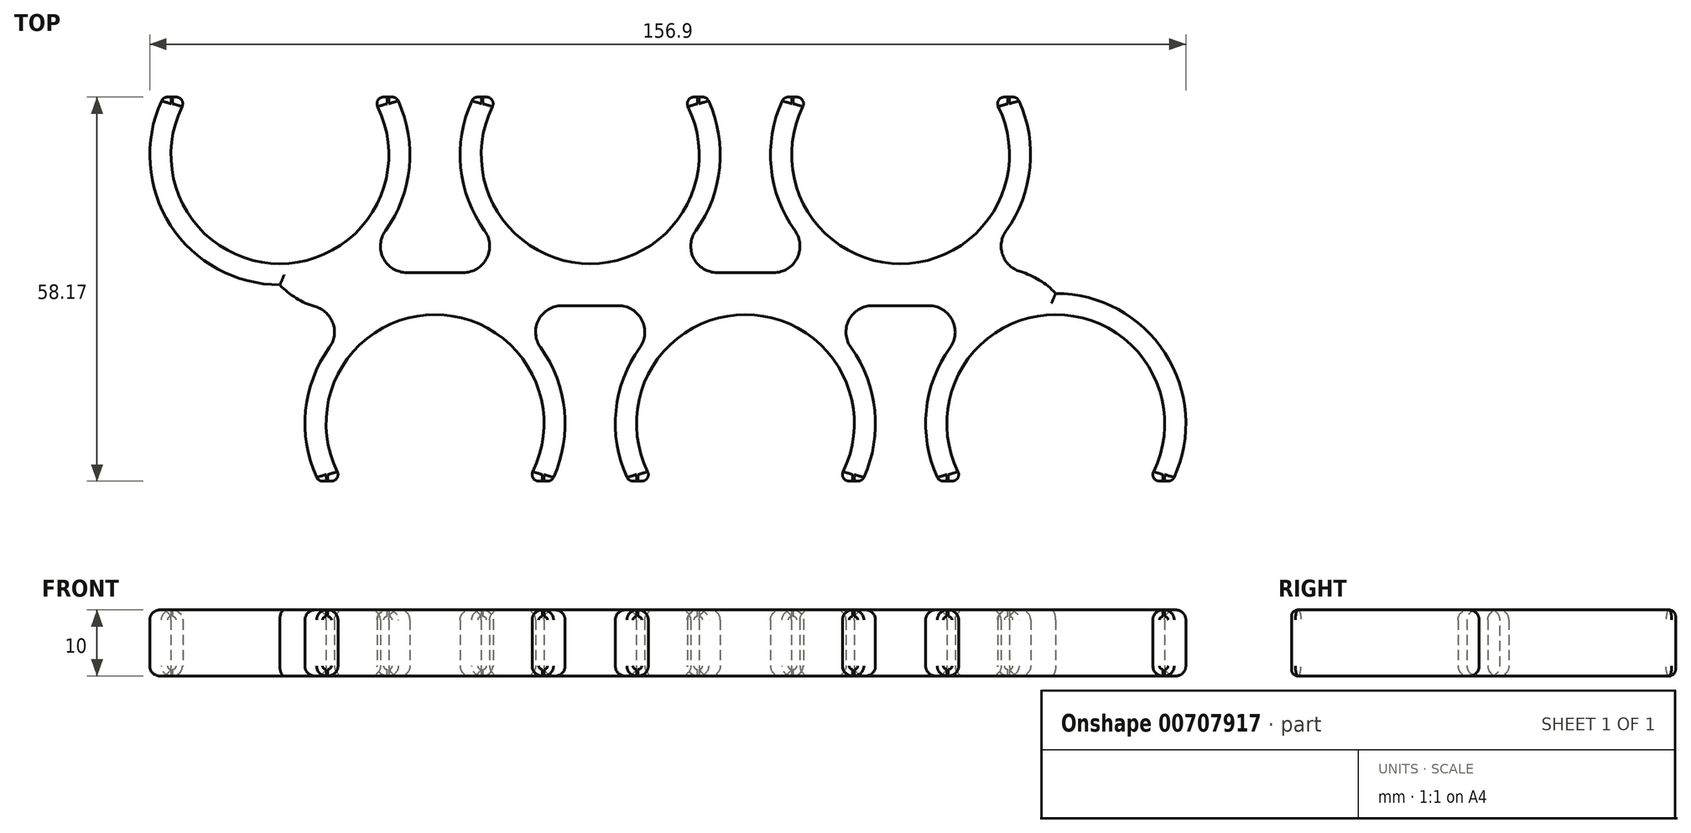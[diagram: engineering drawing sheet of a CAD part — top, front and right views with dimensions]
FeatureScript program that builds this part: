
annotation { "Feature Type Name" : "Feature", "Feature Type Description" : "" }
export const myFeature = defineFeature(function(context is Context, id is Id, definition is map)
    precondition{}
    {
        {
            var Q0;
            Q0=qCreatedBy(makeId("Top.planeOp"),FACE);
            var sketch = newSketch(context, id + "F0", { "sketchPlane" : qUnion([Q0])});
            skArc(sketch, "E0", {"start": v(14, -8.73) * mm, "mid": v(0, 16.5) * mm, "end": v(-14, -8.73) * mm});
            skArc(sketch, "E1", {"start": v(17.66, -8.73) * mm, "mid": v(0, 19.7) * mm, "end": v(-17.66, -8.73) * mm});
            skLineSegment(sketch, "E2", {"start": v(-17.66, -8.73) * mm, "end": v(-14, -8.73) * mm});
            skLineSegment(sketch, "E3", {"start": v(14, -8.73) * mm, "end": v(17.66, -8.73) * mm});
            skArc(sketch, "E4", {"start": v(61, -8.73) * mm, "mid": v(47, 16.5) * mm, "end": v(33, -8.73) * mm});
            skArc(sketch, "E5", {"start": v(64.66, -8.73) * mm, "mid": v(47, 19.7) * mm, "end": v(29.34, -8.73) * mm});
            skLineSegment(sketch, "E6", {"start": v(29.34, -8.73) * mm, "end": v(33, -8.73) * mm});
            skLineSegment(sketch, "E7", {"start": v(61, -8.73) * mm, "end": v(64.66, -8.73) * mm});
            skLineSegment(sketch, "E8", {"start": v(0, 0) * mm, "end": v(47, 0) * mm, "construction": true});
            skArc(sketch, "E9", {"start": v(9.5, 49.44) * mm, "mid": v(23.5, 24.2) * mm, "end": v(37.5, 49.44) * mm});
            skArc(sketch, "E10", {"start": v(5.84, 49.44) * mm, "mid": v(23.5, 21) * mm, "end": v(41.16, 49.44) * mm});
            skLineSegment(sketch, "E11", {"start": v(41.16, 49.44) * mm, "end": v(37.5, 49.44) * mm});
            skLineSegment(sketch, "E12", {"start": v(9.5, 49.44) * mm, "end": v(5.84, 49.44) * mm});
            skLineSegment(sketch, "E13", {"start": v(47, 0) * mm, "end": v(23.5, 40.7) * mm, "construction": true});
            skLineSegment(sketch, "E14", {"start": v(23.5, 40.7) * mm, "end": v(0, 0) * mm, "construction": true});
            skArc(sketch, "E15", {"start": v(-33, -8.73) * mm, "mid": v(-47, 16.5) * mm, "end": v(-61, -8.73) * mm});
            skArc(sketch, "E16", {"start": v(-29.34, -8.73) * mm, "mid": v(-47, 19.7) * mm, "end": v(-64.66, -8.73) * mm});
            skLineSegment(sketch, "E17", {"start": v(-64.66, -8.73) * mm, "end": v(-61, -8.73) * mm});
            skLineSegment(sketch, "E18", {"start": v(-33, -8.73) * mm, "end": v(-29.34, -8.73) * mm});
            skLineSegment(sketch, "E19", {"start": v(-47, 0) * mm, "end": v(0, 0) * mm, "construction": true});
            skArc(sketch, "E20", {"start": v(-37.5, 49.44) * mm, "mid": v(-23.5, 24.2) * mm, "end": v(-9.5, 49.44) * mm});
            skArc(sketch, "E21", {"start": v(-41.16, 49.44) * mm, "mid": v(-23.5, 21) * mm, "end": v(-5.84, 49.44) * mm});
            skLineSegment(sketch, "E22", {"start": v(-5.84, 49.44) * mm, "end": v(-9.5, 49.44) * mm});
            skLineSegment(sketch, "E23", {"start": v(-37.5, 49.44) * mm, "end": v(-41.16, 49.44) * mm});
            skLineSegment(sketch, "E24", {"start": v(23.5, 40.7) * mm, "end": v(-23.5, 40.7) * mm, "construction": true});
            skArc(sketch, "E25", {"start": v(-84.5, 49.44) * mm, "mid": v(-70.5, 24.2) * mm, "end": v(-56.5, 49.44) * mm});
            skArc(sketch, "E26", {"start": v(-88.16, 49.44) * mm, "mid": v(-70.5, 21) * mm, "end": v(-52.84, 49.44) * mm});
            skLineSegment(sketch, "E27", {"start": v(-52.84, 49.44) * mm, "end": v(-56.5, 49.44) * mm});
            skLineSegment(sketch, "E28", {"start": v(-84.5, 49.44) * mm, "end": v(-88.16, 49.44) * mm});
            skLineSegment(sketch, "E29", {"start": v(-23.5, 40.7) * mm, "end": v(-70.5, 40.7) * mm, "construction": true});
            skLineSegment(sketch, "E30", {"start": v(-84.5, 49.44) * mm, "end": v(-56.5, 49.44) * mm, "construction": true});
            skLineSegment(sketch, "E31", {"start": v(-37.5, 49.44) * mm, "end": v(-9.5, 49.44) * mm, "construction": true});
            skLineSegment(sketch, "E32", {"start": v(9.5, 49.44) * mm, "end": v(37.5, 49.44) * mm, "construction": true});
            skLineSegment(sketch, "E33", {"start": v(-61, -8.73) * mm, "end": v(-33, -8.73) * mm, "construction": true});
            skLineSegment(sketch, "E34", {"start": v(-14, -8.73) * mm, "end": v(14, -8.73) * mm, "construction": true});
            skLineSegment(sketch, "E35", {"start": v(33, -8.73) * mm, "end": v(61, -8.73) * mm, "construction": true});
            skCircle(sketch, "E36", {"center": v(-47, 0) * mm, "radius": 16.5 * mm, "construction": true});
            skCircle(sketch, "E37", {"center": v(-47, 0) * mm, "radius": 19.7 * mm, "construction": true});
            skSolve(sketch);
        }
        {
            var Q0;
            Q0 = qSketchRegion(id + "F0", true);
            extrude(context, id + "F1", {"entities" : qUnion([Q0]), "depth" : 10 * mm, "offsetDistance" : 25 * mm});
        }
        {
            var Q0;
            Q0=makeQuery(id+"F1.opExtrude","CAP_FACE",FACE,{"disambiguationData":[OSD([sQuery(id+"F0.wireOp",EDGE,"E15"),sQuery(id+"F0.wireOp",EDGE,"E16"),sQuery(id+"F0.wireOp",EDGE,"E17"),sQuery(id+"F0.wireOp",EDGE,"E18")])],"isStart":false});
            var sketch = newSketch(context, id + "F2", { "sketchPlane" : qUnion([Q0])});
            skLineSegment(sketch, "E38.bottom", {"start": v(-70.5, 22.85) * mm, "end": v(47, 22.85) * mm});
            skLineSegment(sketch, "E38.top", {"start": v(-70.5, 17.85) * mm, "end": v(47, 17.85) * mm});
            skLineSegment(sketch, "E38.left", {"start": v(-70.5, 22.85) * mm, "end": v(-70.5, 17.85) * mm});
            skLineSegment(sketch, "E38.right", {"start": v(47, 22.85) * mm, "end": v(47, 17.85) * mm});
            skLineSegment(sketch, "E39", {"start": v(0, 16.5) * mm, "end": v(0, 17.85) * mm, "construction": true});
            skLineSegment(sketch, "E40", {"start": v(23.5, 24.2) * mm, "end": v(23.5, 22.85) * mm, "construction": true});
            skSolve(sketch);
        }
        {
            var Q0;
            Q0 = qSketchRegion(id + "F2", true);
            extrude(context, id + "F3", {"entities" : qUnion([Q0]), "operationType" : NewBodyOperationType.ADD, "oppositeDirection" : true, "depth" : 10 * mm, "offsetDistance" : 25 * mm});
        }
        {
            var Q0;
            Q0=makeQuery(id+"F3.boolean.opBoolean","INTERSECT",EDGE,{"disambiguationData":[OD(0.0)],"derivedFrom":[makeQuery(id+"F1.opExtrude","SWEPT_FACE",FACE,{"disambiguationData":[OSD([sQuery(id+"F0.wireOp",EDGE,"E21")])]}),makeQuery(id+"F3.opExtrude","SWEPT_FACE",FACE,{"disambiguationData":[OSD([sQuery(id+"F2.wireOp",EDGE,"E38.bottom")])]})]});
            var Q1;
            Q1=makeQuery(id+"F3.boolean.opBoolean","INTERSECT",EDGE,{"disambiguationData":[OD(1.0)],"derivedFrom":[makeQuery(id+"F1.opExtrude","SWEPT_FACE",FACE,{"disambiguationData":[OSD([sQuery(id+"F0.wireOp",EDGE,"E10")])]}),makeQuery(id+"F3.opExtrude","SWEPT_FACE",FACE,{"disambiguationData":[OSD([sQuery(id+"F2.wireOp",EDGE,"E38.bottom")])]})]});
            var Q2;
            Q2=makeQuery(id+"F3.boolean.opBoolean","INTERSECT",EDGE,{"derivedFrom":[makeQuery(id+"F1.opExtrude","SWEPT_FACE",FACE,{"disambiguationData":[OSD([sQuery(id+"F0.wireOp",EDGE,"E5")])]}),makeQuery(id+"F3.opExtrude","SWEPT_FACE",FACE,{"disambiguationData":[OSD([sQuery(id+"F2.wireOp",EDGE,"E38.top")])]})]});
            var Q3;
            Q3=makeQuery(id+"F3.boolean.opBoolean","INTERSECT",EDGE,{"disambiguationData":[OD(1.0)],"derivedFrom":[makeQuery(id+"F1.opExtrude","SWEPT_FACE",FACE,{"disambiguationData":[OSD([sQuery(id+"F0.wireOp",EDGE,"E1")])]}),makeQuery(id+"F3.opExtrude","SWEPT_FACE",FACE,{"disambiguationData":[OSD([sQuery(id+"F2.wireOp",EDGE,"E38.top")])]})]});
            var Q4;
            Q4=makeQuery(id+"F3.boolean.opBoolean","INTERSECT",EDGE,{"disambiguationData":[OD(0.0)],"derivedFrom":[makeQuery(id+"F1.opExtrude","SWEPT_FACE",FACE,{"disambiguationData":[OSD([sQuery(id+"F0.wireOp",EDGE,"E16")])]}),makeQuery(id+"F3.opExtrude","SWEPT_FACE",FACE,{"disambiguationData":[OSD([sQuery(id+"F2.wireOp",EDGE,"E38.top")])]})]});
            var Q5;
            Q5=makeQuery(id+"F3.boolean.opBoolean","INTERSECT",EDGE,{"derivedFrom":[makeQuery(id+"F1.opExtrude","SWEPT_FACE",FACE,{"disambiguationData":[OSD([sQuery(id+"F0.wireOp",EDGE,"E26")])]}),makeQuery(id+"F3.opExtrude","SWEPT_FACE",FACE,{"disambiguationData":[OSD([sQuery(id+"F2.wireOp",EDGE,"E38.bottom")])]})]});
            var Q6;
            Q6=makeQuery(id+"F3.boolean.opBoolean","INTERSECT",EDGE,{"disambiguationData":[OD(1.0)],"derivedFrom":[makeQuery(id+"F1.opExtrude","SWEPT_FACE",FACE,{"disambiguationData":[OSD([sQuery(id+"F0.wireOp",EDGE,"E21")])]}),makeQuery(id+"F3.opExtrude","SWEPT_FACE",FACE,{"disambiguationData":[OSD([sQuery(id+"F2.wireOp",EDGE,"E38.bottom")])]})]});
            var Q7;
            Q7=makeQuery(id+"F3.boolean.opBoolean","INTERSECT",EDGE,{"disambiguationData":[OD(0.0)],"derivedFrom":[makeQuery(id+"F1.opExtrude","SWEPT_FACE",FACE,{"disambiguationData":[OSD([sQuery(id+"F0.wireOp",EDGE,"E10")])]}),makeQuery(id+"F3.opExtrude","SWEPT_FACE",FACE,{"disambiguationData":[OSD([sQuery(id+"F2.wireOp",EDGE,"E38.bottom")])]})]});
            var Q8;
            Q8=makeQuery(id+"F3.boolean.opBoolean","INTERSECT",EDGE,{"disambiguationData":[OD(0.0)],"derivedFrom":[makeQuery(id+"F1.opExtrude","SWEPT_FACE",FACE,{"disambiguationData":[OSD([sQuery(id+"F0.wireOp",EDGE,"E1")])]}),makeQuery(id+"F3.opExtrude","SWEPT_FACE",FACE,{"disambiguationData":[OSD([sQuery(id+"F2.wireOp",EDGE,"E38.top")])]})]});
            var Q9;
            Q9=makeQuery(id+"F3.boolean.opBoolean","INTERSECT",EDGE,{"disambiguationData":[OD(1.0)],"derivedFrom":[makeQuery(id+"F1.opExtrude","SWEPT_FACE",FACE,{"disambiguationData":[OSD([sQuery(id+"F0.wireOp",EDGE,"E16")])]}),makeQuery(id+"F3.opExtrude","SWEPT_FACE",FACE,{"disambiguationData":[OSD([sQuery(id+"F2.wireOp",EDGE,"E38.top")])]})]});
            fillet(context, id + "F4", {"entities" : qUnion([Q0, Q1, Q2, Q3, Q4, Q5, Q6, Q7, Q8, Q9]), "radius" : 4 * mm, "tangentPropagation" : true, "allowEdgeOverflow" : false});
        }
        {
            var Q0;
            Q0=makeQuery(id+"F1.opExtrude","SWEPT_FACE",FACE,{"disambiguationData":[OSD([sQuery(id+"F0.wireOp",EDGE,"E28")])]});
            var Q1;
            Q1=makeQuery(id+"F1.opExtrude","SWEPT_FACE",FACE,{"disambiguationData":[OSD([sQuery(id+"F0.wireOp",EDGE,"E27")])]});
            var Q2;
            Q2=makeQuery(id+"F1.opExtrude","SWEPT_FACE",FACE,{"disambiguationData":[OSD([sQuery(id+"F0.wireOp",EDGE,"E23")])]});
            var Q3;
            Q3=makeQuery(id+"F1.opExtrude","SWEPT_FACE",FACE,{"disambiguationData":[OSD([sQuery(id+"F0.wireOp",EDGE,"E22")])]});
            var Q4;
            Q4=makeQuery(id+"F1.opExtrude","SWEPT_FACE",FACE,{"disambiguationData":[OSD([sQuery(id+"F0.wireOp",EDGE,"E12")])]});
            var Q5;
            Q5=makeQuery(id+"F1.opExtrude","SWEPT_FACE",FACE,{"disambiguationData":[OSD([sQuery(id+"F0.wireOp",EDGE,"E11")])]});
            var Q6;
            Q6=makeQuery(id+"F1.opExtrude","SWEPT_FACE",FACE,{"disambiguationData":[OSD([sQuery(id+"F0.wireOp",EDGE,"E7")])]});
            var Q7;
            Q7=makeQuery(id+"F1.opExtrude","SWEPT_FACE",FACE,{"disambiguationData":[OSD([sQuery(id+"F0.wireOp",EDGE,"E6")])]});
            var Q8;
            Q8=makeQuery(id+"F1.opExtrude","SWEPT_FACE",FACE,{"disambiguationData":[OSD([sQuery(id+"F0.wireOp",EDGE,"E3")])]});
            var Q9;
            Q9=makeQuery(id+"F1.opExtrude","SWEPT_FACE",FACE,{"disambiguationData":[OSD([sQuery(id+"F0.wireOp",EDGE,"E2")])]});
            var Q10;
            Q10=makeQuery(id+"F1.opExtrude","SWEPT_FACE",FACE,{"disambiguationData":[OSD([sQuery(id+"F0.wireOp",EDGE,"E18")])]});
            var Q11;
            Q11=makeQuery(id+"F1.opExtrude","SWEPT_FACE",FACE,{"disambiguationData":[OSD([sQuery(id+"F0.wireOp",EDGE,"E17")])]});
            fillet(context, id + "F5", {"entities" : qUnion([Q0, Q1, Q2, Q3, Q4, Q5, Q6, Q7, Q8, Q9, Q10, Q11]), "radius" : 1 * mm, "tangentPropagation" : true, "allowEdgeOverflow" : false});
        }
        {
            var Q0;
            Q0=makeQuery(id+"F3.opExtrude","SWEPT_EDGE",EDGE,{"disambiguationData":[OSD([sQuery(id+"F2.wireOp",EDGE,"E38.top"),sQuery(id+"F2.wireOp",EDGE,"E38.left")])]});
            var Q1;
            Q1=makeQuery(id+"F3.opExtrude","SWEPT_EDGE",EDGE,{"disambiguationData":[OSD([sQuery(id+"F2.wireOp",EDGE,"E38.bottom"),sQuery(id+"F2.wireOp",EDGE,"E38.right")])]});
            fillet(context, id + "F6", {"entities" : qUnion([Q0, Q1]), "radius" : 12 * mm, "tangentPropagation" : true, "allowEdgeOverflow" : false});
        }
        {
            var Q0;
            Q0=makeQuery(id+"F3.boolean.opBoolean","MERGE",FACE,{"derivedFrom":[makeQuery(id+"F1.opExtrude","CAP_FACE",FACE,{"disambiguationData":[OSD([sQuery(id+"F0.wireOp",EDGE,"E0"),sQuery(id+"F0.wireOp",EDGE,"E1"),sQuery(id+"F0.wireOp",EDGE,"E2"),sQuery(id+"F0.wireOp",EDGE,"E3")])],"isStart":false}),makeQuery(id+"F1.opExtrude","CAP_FACE",FACE,{"disambiguationData":[OSD([sQuery(id+"F0.wireOp",EDGE,"E4"),sQuery(id+"F0.wireOp",EDGE,"E5"),sQuery(id+"F0.wireOp",EDGE,"E6"),sQuery(id+"F0.wireOp",EDGE,"E7")])],"isStart":false}),makeQuery(id+"F1.opExtrude","CAP_FACE",FACE,{"disambiguationData":[OSD([sQuery(id+"F0.wireOp",EDGE,"E9"),sQuery(id+"F0.wireOp",EDGE,"E10"),sQuery(id+"F0.wireOp",EDGE,"E11"),sQuery(id+"F0.wireOp",EDGE,"E12")])],"isStart":false}),makeQuery(id+"F1.opExtrude","CAP_FACE",FACE,{"disambiguationData":[OSD([sQuery(id+"F0.wireOp",EDGE,"E15"),sQuery(id+"F0.wireOp",EDGE,"E16"),sQuery(id+"F0.wireOp",EDGE,"E17"),sQuery(id+"F0.wireOp",EDGE,"E18")])],"isStart":false}),makeQuery(id+"F1.opExtrude","CAP_FACE",FACE,{"disambiguationData":[OSD([sQuery(id+"F0.wireOp",EDGE,"E20"),sQuery(id+"F0.wireOp",EDGE,"E21"),sQuery(id+"F0.wireOp",EDGE,"E22"),sQuery(id+"F0.wireOp",EDGE,"E23")])],"isStart":false}),makeQuery(id+"F1.opExtrude","CAP_FACE",FACE,{"disambiguationData":[OSD([sQuery(id+"F0.wireOp",EDGE,"E25"),sQuery(id+"F0.wireOp",EDGE,"E26"),sQuery(id+"F0.wireOp",EDGE,"E27"),sQuery(id+"F0.wireOp",EDGE,"E28")])],"isStart":false}),makeQuery(id+"F3.opExtrude","CAP_FACE",FACE,{"disambiguationData":[OSD([sQuery(id+"F2.wireOp",EDGE,"E38.bottom"),sQuery(id+"F2.wireOp",EDGE,"E38.top"),sQuery(id+"F2.wireOp",EDGE,"E38.left"),sQuery(id+"F2.wireOp",EDGE,"E38.right")])],"isStart":true})]});
            var Q1;
            Q1=makeQuery(id+"F3.boolean.opBoolean","MERGE",FACE,{"derivedFrom":[makeQuery(id+"F1.opExtrude","CAP_FACE",FACE,{"disambiguationData":[OSD([sQuery(id+"F0.wireOp",EDGE,"E0"),sQuery(id+"F0.wireOp",EDGE,"E1"),sQuery(id+"F0.wireOp",EDGE,"E2"),sQuery(id+"F0.wireOp",EDGE,"E3")])],"isStart":true}),makeQuery(id+"F1.opExtrude","CAP_FACE",FACE,{"disambiguationData":[OSD([sQuery(id+"F0.wireOp",EDGE,"E4"),sQuery(id+"F0.wireOp",EDGE,"E5"),sQuery(id+"F0.wireOp",EDGE,"E6"),sQuery(id+"F0.wireOp",EDGE,"E7")])],"isStart":true}),makeQuery(id+"F1.opExtrude","CAP_FACE",FACE,{"disambiguationData":[OSD([sQuery(id+"F0.wireOp",EDGE,"E9"),sQuery(id+"F0.wireOp",EDGE,"E10"),sQuery(id+"F0.wireOp",EDGE,"E11"),sQuery(id+"F0.wireOp",EDGE,"E12")])],"isStart":true}),makeQuery(id+"F1.opExtrude","CAP_FACE",FACE,{"disambiguationData":[OSD([sQuery(id+"F0.wireOp",EDGE,"E15"),sQuery(id+"F0.wireOp",EDGE,"E16"),sQuery(id+"F0.wireOp",EDGE,"E17"),sQuery(id+"F0.wireOp",EDGE,"E18")])],"isStart":true}),makeQuery(id+"F1.opExtrude","CAP_FACE",FACE,{"disambiguationData":[OSD([sQuery(id+"F0.wireOp",EDGE,"E20"),sQuery(id+"F0.wireOp",EDGE,"E21"),sQuery(id+"F0.wireOp",EDGE,"E22"),sQuery(id+"F0.wireOp",EDGE,"E23")])],"isStart":true}),makeQuery(id+"F1.opExtrude","CAP_FACE",FACE,{"disambiguationData":[OSD([sQuery(id+"F0.wireOp",EDGE,"E25"),sQuery(id+"F0.wireOp",EDGE,"E26"),sQuery(id+"F0.wireOp",EDGE,"E27"),sQuery(id+"F0.wireOp",EDGE,"E28")])],"isStart":true}),makeQuery(id+"F3.opExtrude","CAP_FACE",FACE,{"disambiguationData":[OSD([sQuery(id+"F2.wireOp",EDGE,"E38.bottom"),sQuery(id+"F2.wireOp",EDGE,"E38.top"),sQuery(id+"F2.wireOp",EDGE,"E38.left"),sQuery(id+"F2.wireOp",EDGE,"E38.right")])],"isStart":false})]});
            fillet(context, id + "F7", {"entities" : qUnion([Q0, Q1]), "radius" : 1.5 * mm, "tangentPropagation" : true, "allowEdgeOverflow" : false});
        }
    });
